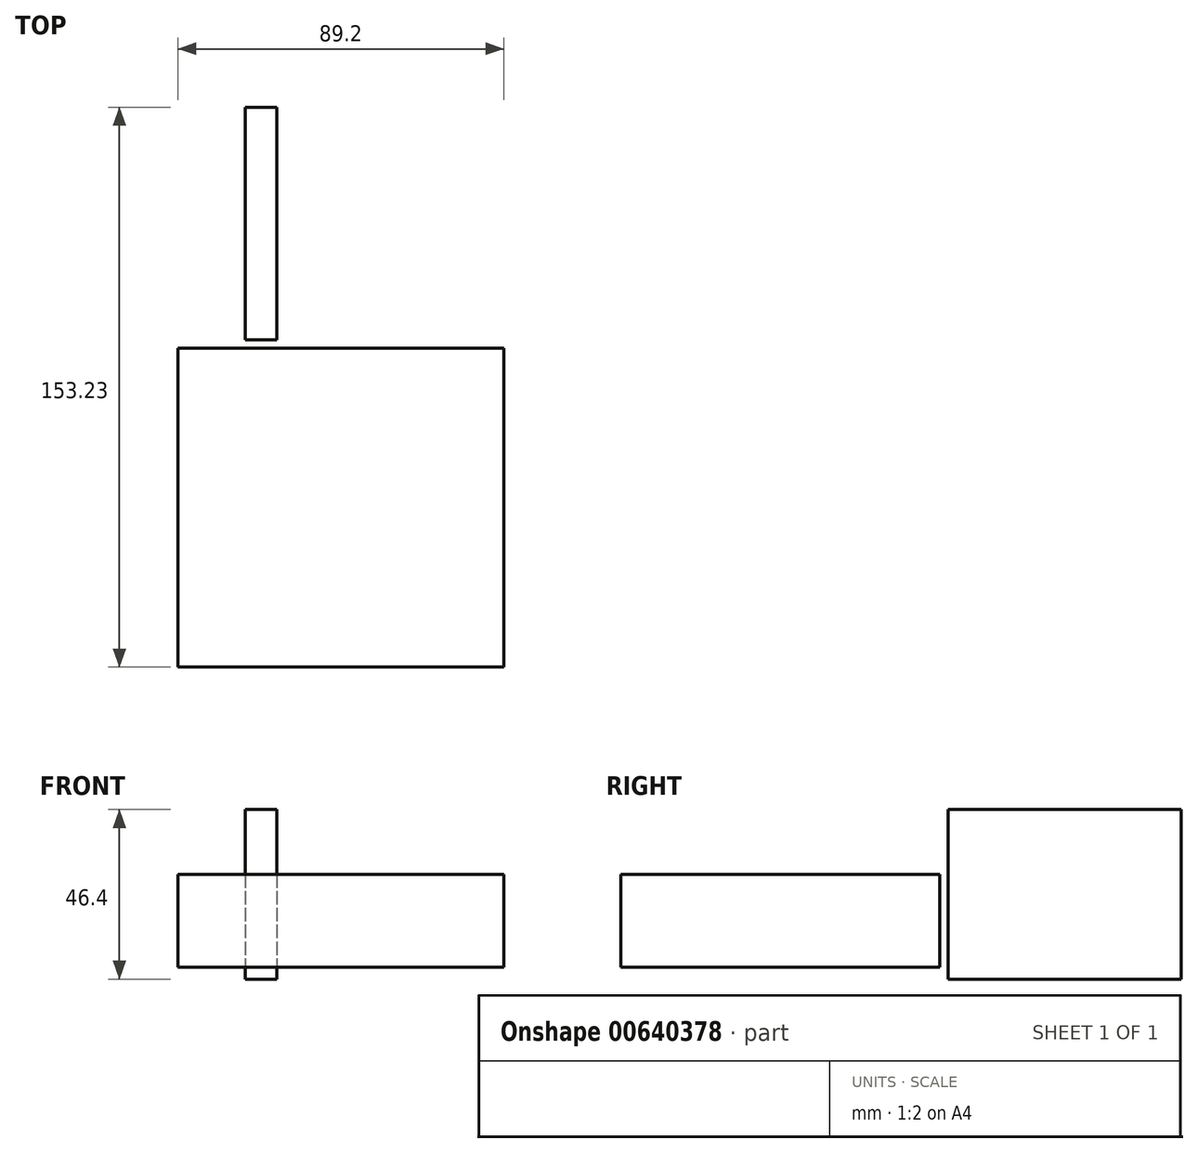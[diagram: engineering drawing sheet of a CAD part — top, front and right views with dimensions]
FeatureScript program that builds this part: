
annotation { "Feature Type Name" : "Feature", "Feature Type Description" : "" }
export const myFeature = defineFeature(function(context is Context, id is Id, definition is map)
    precondition{}
    {
        {
            var Q0;
            Q0=qCreatedBy(makeId("Top.planeOp"),FACE);
            var sketch = newSketch(context, id + "F0", { "sketchPlane" : qUnion([Q0])});
            skLineSegment(sketch, "E0.bottom", {"start": v(-27.08, -112.32) * mm, "end": v(62.12, -112.32) * mm});
            skLineSegment(sketch, "E0.top", {"start": v(-27.08, -25.1) * mm, "end": v(62.12, -25.1) * mm});
            skLineSegment(sketch, "E0.left", {"start": v(-27.08, -112.32) * mm, "end": v(-27.08, -25.1) * mm});
            skLineSegment(sketch, "E0.right", {"start": v(62.12, -112.32) * mm, "end": v(62.12, -25.1) * mm});
            skSolve(sketch);
        }
        {
            var Q0;
            Q0=makeQuery(id+"F0.imprint","IMPRINT",FACE,{"disambiguationData":[TD([[makeQuery(id+"F0.imprint","IMPRINT",EDGE,{"derivedFrom":sQuery(id+"F0.wireOp",EDGE,"E0.bottom")}),1.0]])]});
            extrude(context, id + "F1", {"entities" : qUnion([Q0]), "depth" : 25.4 * mm, "offsetDistance" : 25.4 * mm});
        }
        {
            var Q0;
            Q0=qCreatedBy(makeId("Right.planeOp"),FACE);
            var sketch = newSketch(context, id + "F2", { "sketchPlane" : qUnion([Q0])});
            skLineSegment(sketch, "E1.bottom", {"start": v(-22.82, 43.1) * mm, "end": v(40.91, 43.1) * mm});
            skLineSegment(sketch, "E1.top", {"start": v(-22.82, -3.3) * mm, "end": v(40.91, -3.3) * mm});
            skLineSegment(sketch, "E1.left", {"start": v(-22.82, 43.1) * mm, "end": v(-22.82, -3.3) * mm});
            skLineSegment(sketch, "E1.right", {"start": v(40.91, 43.1) * mm, "end": v(40.91, -3.3) * mm});
            skSolve(sketch);
        }
        {
            var Q0;
            Q0 = qSketchRegion(id + "F2", true);
            extrude(context, id + "F3", {"entities" : qUnion([Q0]), "oppositeDirection" : true, "depth" : 8.64 * mm, "offsetDistance" : 25.4 * mm});
        }
    });
